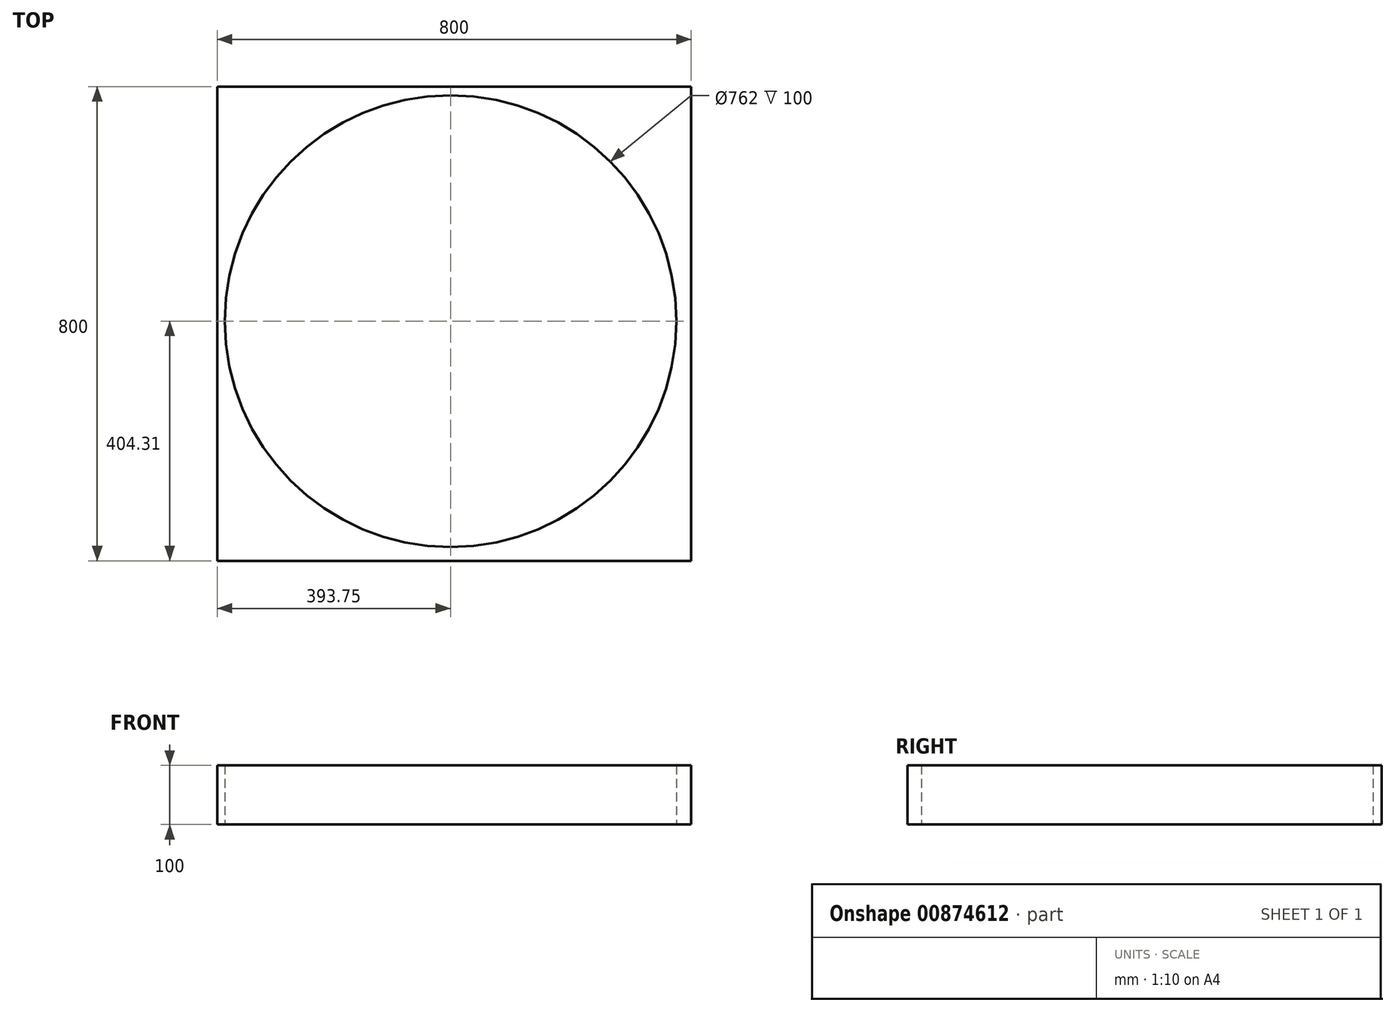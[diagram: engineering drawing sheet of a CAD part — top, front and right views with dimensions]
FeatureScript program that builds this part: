
annotation { "Feature Type Name" : "Feature", "Feature Type Description" : "" }
export const myFeature = defineFeature(function(context is Context, id is Id, definition is map)
    precondition{}
    {
        {
            var Q0;
            Q0=qCreatedBy(makeId("Top.planeOp"),FACE);
            var sketch = newSketch(context, id + "F0", { "sketchPlane" : qUnion([Q0])});
            skCircle(sketch, "E0", {"center": v(0, 0) * mm, "radius": 381 * mm});
            skLineSegment(sketch, "E1.bottom", {"start": v(-393.75, -404.3) * mm, "end": v(406.25, -404.3) * mm});
            skLineSegment(sketch, "E1.top", {"start": v(-393.75, 395.7) * mm, "end": v(406.25, 395.7) * mm});
            skLineSegment(sketch, "E1.left", {"start": v(-393.75, -404.3) * mm, "end": v(-393.75, 395.7) * mm});
            skLineSegment(sketch, "E1.right", {"start": v(406.25, -404.3) * mm, "end": v(406.25, 395.7) * mm});
            skSolve(sketch);
        }
        {
            var Q0;
            Q0=makeQuery(id+"F0.imprint","IMPRINT",FACE,{"disambiguationData":[TD([[makeQuery(id+"F0.imprint","IMPRINT",EDGE,{"derivedFrom":sQuery(id+"F0.wireOp",EDGE,"E0")}),-1.0]])]});
            extrude(context, id + "F1", {"entities" : qUnion([Q0]), "depth" : 100 * mm, "offsetDistance" : 25 * mm});
        }
    });
